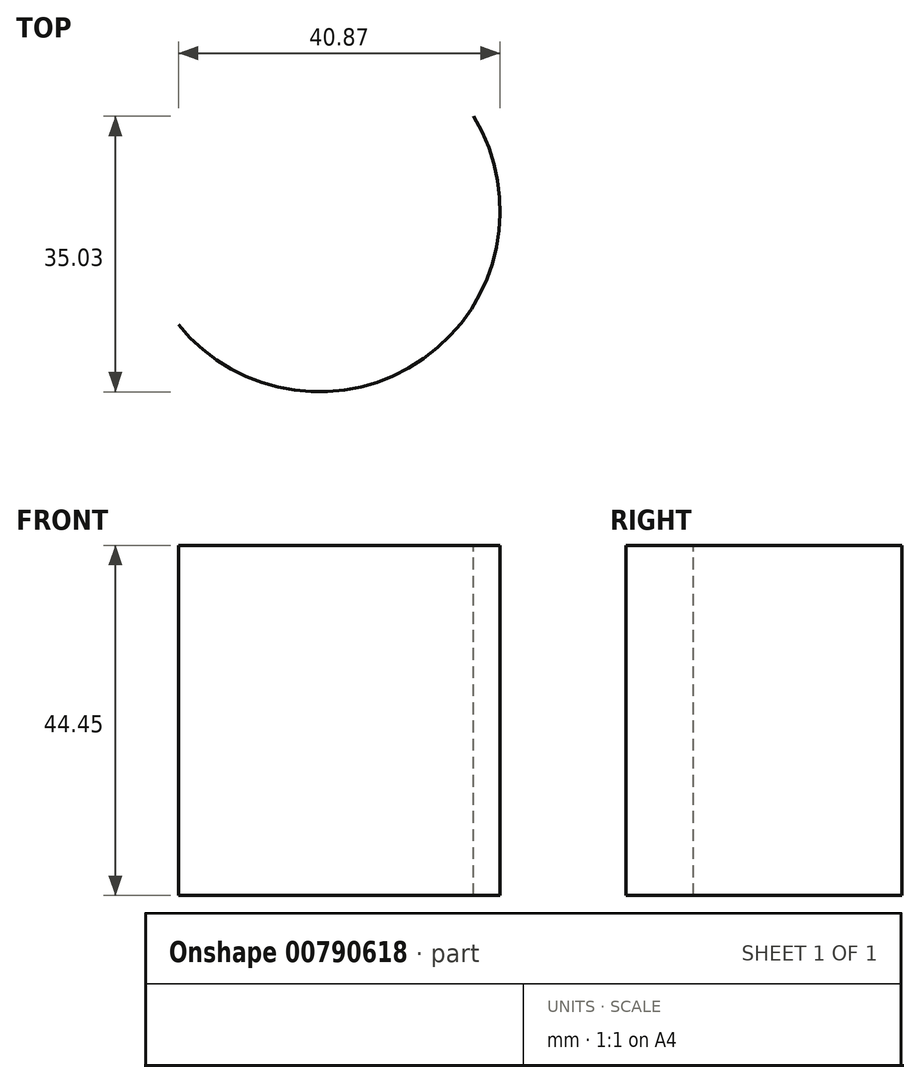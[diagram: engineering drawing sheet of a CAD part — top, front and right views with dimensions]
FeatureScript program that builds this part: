
annotation { "Feature Type Name" : "Feature", "Feature Type Description" : "" }
export const myFeature = defineFeature(function(context is Context, id is Id, definition is map)
    precondition{}
    {
        {
            var Q0;
            Q0=qCreatedBy(makeId("Top.planeOp"),FACE);
            var sketch = newSketch(context, id + "F0", { "sketchPlane" : qUnion([Q0])});
            skArc(sketch, "E0", {"start": v(0, 0) * mm, "mid": v(31.15, -4.3) * mm, "end": v(37.47, 26.5) * mm});
            skSolve(sketch);
        }
        {
            var Q0;
            Q0=sQuery(id+"F0.wireOp",EDGE,"E0");
            extrude(context, id + "F1", {"bodyType" : ToolBodyType.SURFACE, "surfaceEntities" : qUnion([Q0]), "depth" : 44.45 * mm, "offsetDistance" : 25.4 * mm});
        }
    });
